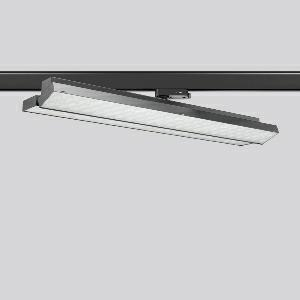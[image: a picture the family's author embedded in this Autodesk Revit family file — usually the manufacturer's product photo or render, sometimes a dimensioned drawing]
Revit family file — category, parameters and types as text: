
# Revit family: tx-move_742162_003_1_1a39
name_source: partatom
category: Lighting Fixtures
units: mm (PartAtom-declared; Revit-internal decimal feet)

## family parameters
Cut with Voids When Loaded = No
Host = Face
Light Source = No
Part Type = Normal
Room Calculation Point = No
Round Connector Dimension = Use Diameter
Shared = No

## types (1)
- MultiLumen 1 (1 x LED Modul 840, 3150 lm, 4000)
    Apparent Load = 41 VA
    CIE Flux Codes = 77 96 99 100 100
    Color Rendering = 80
    Color Temperature = 4000
    Default Elevation = 1800 mm
    Description = Series: TX-MOVE
Multifunctional surface-mounted spotlight for area lighting. Very flat design. Housing: sheet steel, powder-coated. Rotation range: 356°. Swivel range: 90°. Consistent alignment possible with visible tilt scale. High-efficiency LED units with optimum light control thanks to clear plastic (PC) lens optics. Spezielle Mikrostrukturen reduzieren Gelbsaum. Symmetrical light distribution. With multi adaptor for 3-circuit tracks 230 V. Suitable for Track on ceiling. MultiLumen: Luminous flux adjustable in 3 steps. Factory setting is the highest luminous flux. Environmentally friendly and resource-saving due to replaceable and recyclable components. 
Colour: deep black, matt (RAL 9005)
Length: 570 mm
Width: 119 mm
Height: 92 mm
Lamp: LED
Socket: without socket
Colour temperature: 4000K
Colour rendering index (CRI): 80
System power: 41 W
Rated luminous flux: 6300 lm
Luminous efficiency: 154 lm/W
System power 2: 57 W
Rated luminous flux 2: 8550 lm
Luminous efficiency 2: 150 lm/W
System power 3: 73 W
Rated luminous flux 3: 10400 lm
Luminous efficiency 3: 142 lm/W
Control gear: Regulated power supply
Protection class: I
Type of protection: IP 20
    Height = 75 mm
    Lamp = 1 x LED Modul 840
    Lamp Light Flux = 3150 lm
    Lamp count = 1
    Length = 569 mm
    Lifetime = 50000 h
    Luminous efficacy = 154 lm/W
    Manufacturer = RZB
    ModVariant = No
    Model = 742162.003.1
    Mounting Place = Ceiling
    Mounting Type = Surface mounted
    Number of Poles = 1
    OnlyDefault = Yes
    Power Factor = 1
    Product Name = TX-MOVE
    Product group = Track mounted projectors
    ProductGroupID = 301
    Protection Class = Protection class I
    Protection Degree = IP 20
    RLX_Detail_Level = 1
    RLX_Emergency_Light_Flux = 0 lm
    RLX_Emergency_Type = 0
    RLX_Emergency_Type_DB = No
    RlxData = <blob elided: 36765 chars, md5=8470f71c>
    Socket = socket
    Standby Power = 0 W
    System Light Flux = 6300 lm
    System Power = 41 W
    Type Comments = MultiLumen 1
    Type Image = 742162.003.jpg
    URL = http://relux.com
    VarID = multilumen_1
    Voltage = 0 V
    Weight = 0.00 kg
    Width = 119 mm

## geometry (parser evidence)
native form markers: Blend x4, Sweep x14
no freeform markers — native parametric forms only
